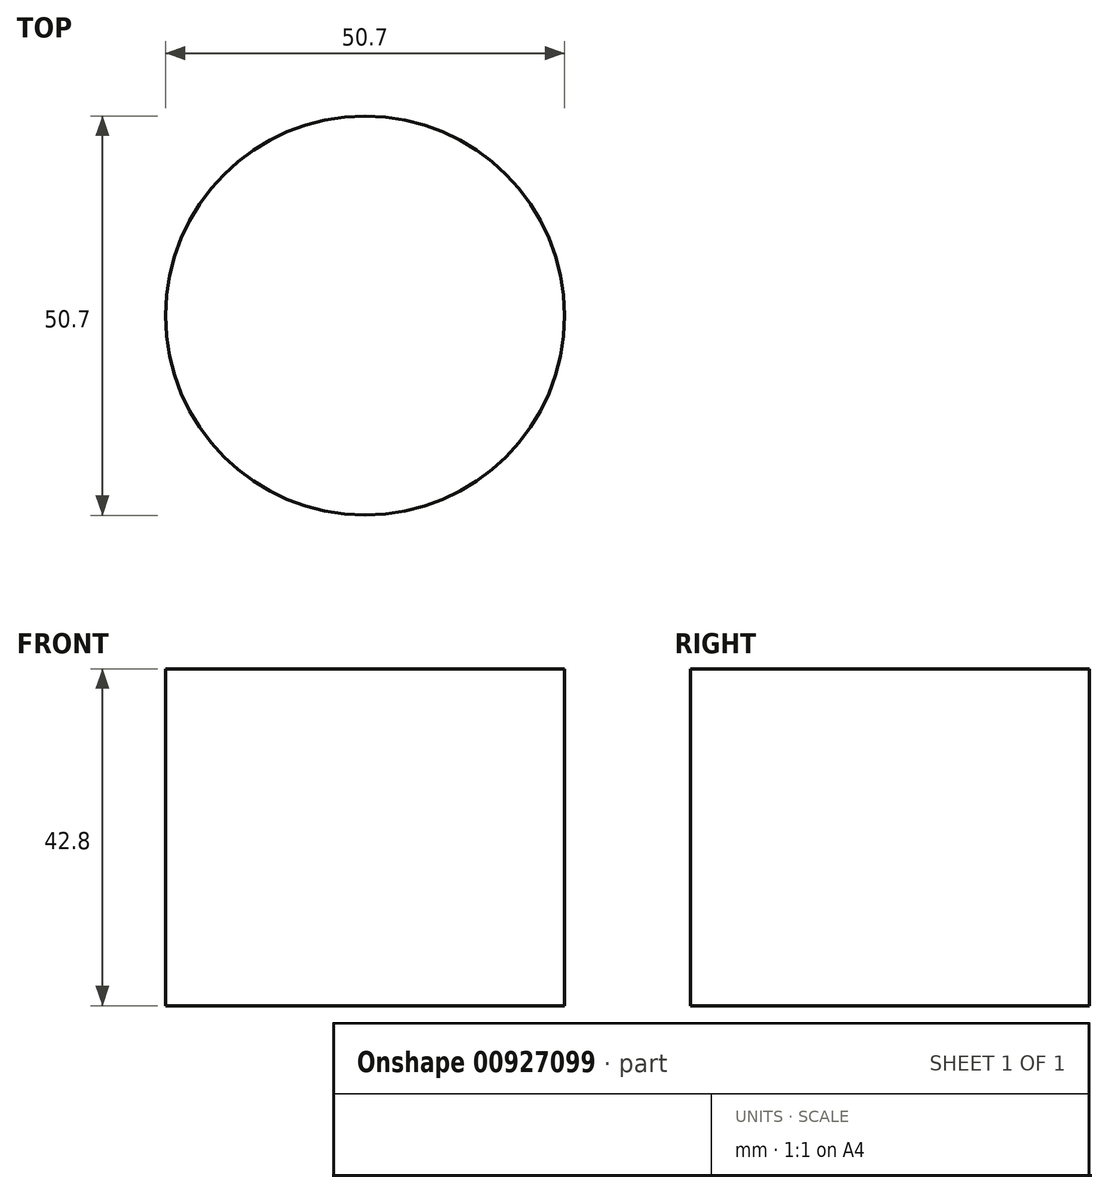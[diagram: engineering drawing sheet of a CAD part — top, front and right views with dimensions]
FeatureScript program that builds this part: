
annotation { "Feature Type Name" : "Feature", "Feature Type Description" : "" }
export const myFeature = defineFeature(function(context is Context, id is Id, definition is map)
    precondition{}
    {
        {
            var Q0;
            Q0=qCreatedBy(makeId("Top.planeOp"),FACE);
            var sketch = newSketch(context, id + "F0", { "sketchPlane" : qUnion([Q0])});
            skCircle(sketch, "E0", {"center": v(-10.87, 2.87) * mm, "radius": 25.35 * mm});
            skSolve(sketch);
        }
        {
            var Q0;
            Q0=makeQuery(id+"F0.imprint","IMPRINT",FACE,{"disambiguationData":[TD([[makeQuery(id+"F0.imprint","IMPRINT",EDGE,{"derivedFrom":sQuery(id+"F0.wireOp",EDGE,"E0")}),1.0]])]});
            extrude(context, id + "F1", {"entities" : qUnion([Q0]), "oppositeDirection" : true, "depth" : 42.8 * mm, "offsetDistance" : 25 * mm});
        }
    });
